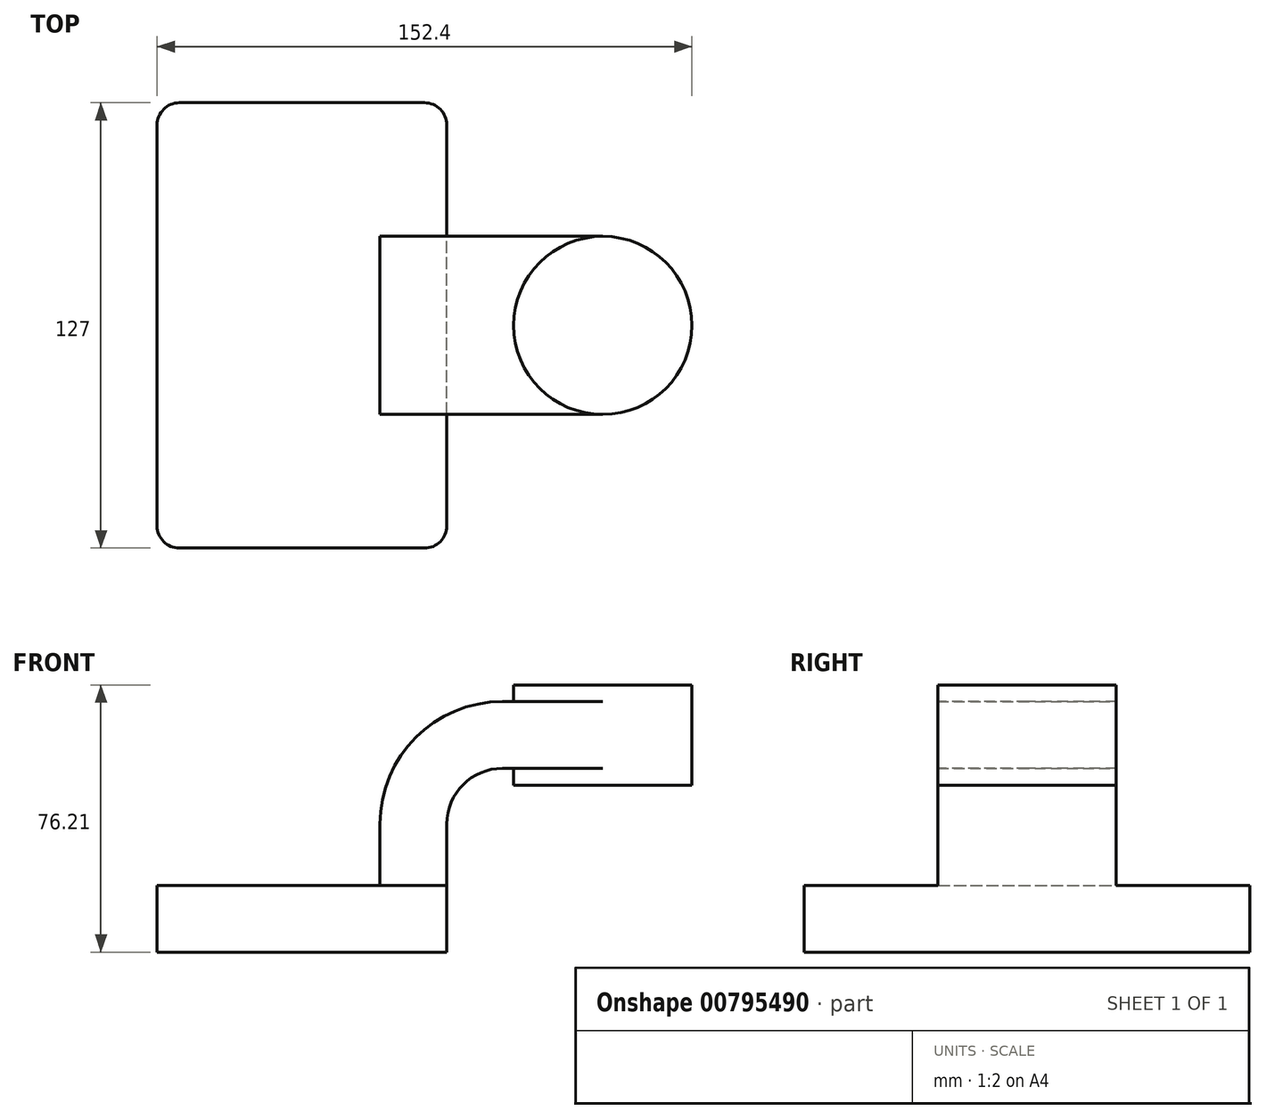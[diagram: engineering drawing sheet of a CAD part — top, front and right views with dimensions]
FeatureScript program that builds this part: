
annotation { "Feature Type Name" : "Feature", "Feature Type Description" : "" }
export const myFeature = defineFeature(function(context is Context, id is Id, definition is map)
    precondition{}
    {
        {
            var Q0;
            Q0=qCreatedBy(makeId("Front.planeOp"),FACE);
            var sketch = newSketch(context, id + "F0", { "sketchPlane" : qUnion([Q0])});
            skLineSegment(sketch, "E0.bottom", {"start": v(-41.28, 9.52) * mm, "end": v(41.27, 9.53) * mm});
            skLineSegment(sketch, "E0.top", {"start": v(-41.27, -9.52) * mm, "end": v(41.28, -9.52) * mm});
            skLineSegment(sketch, "E0.left", {"start": v(-41.28, 9.52) * mm, "end": v(-41.27, -9.53) * mm});
            skLineSegment(sketch, "E0.right", {"start": v(41.28, 9.53) * mm, "end": v(41.28, -9.52) * mm});
            skPoint(sketch, "E0.middle", {"position": v(0, 0) * mm});
            skLineSegment(sketch, "E1.bottom", {"start": v(111.13, 38.1) * mm, "end": v(60.33, 38.1) * mm});
            skLineSegment(sketch, "E1.top", {"start": v(111.13, 66.68) * mm, "end": v(60.33, 66.67) * mm});
            skLineSegment(sketch, "E1.left", {"start": v(111.13, 38.1) * mm, "end": v(111.13, 66.68) * mm});
            skLineSegment(sketch, "E1.right", {"start": v(60.33, 38.1) * mm, "end": v(60.33, 66.68) * mm});
            skPoint(sketch, "E1.middle", {"position": v(85.73, 52.39) * mm});
            skLineSegment(sketch, "E2", {"start": v(41.27, 9.53) * mm, "end": v(41.27, 27) * mm});
            skArc(sketch, "E3", {"start": v(41.27, 27) * mm, "mid": v(45.92, 38.23) * mm, "end": v(57.15, 42.88) * mm});
            skLineSegment(sketch, "E4", {"start": v(57.15, 42.88) * mm, "end": v(85.73, 42.88) * mm});
            skLineSegment(sketch, "E5.0", {"start": v(57.15, 61.93) * mm, "end": v(85.72, 61.93) * mm});
            skArc(sketch, "E5.1", {"start": v(22.23, 27) * mm, "mid": v(32.45, 51.7) * mm, "end": v(57.15, 61.93) * mm});
            skLineSegment(sketch, "E5.2", {"start": v(22.22, 9.53) * mm, "end": v(22.22, 27) * mm});
            skFitSpline(sketch, "E6", {"points": [v(-41.28, 9.52) * mm, v(57.15, 61.93) * mm], "startDerivative": vector(47.12, 132.78) * mm, "endDerivative": vector(118.1, -13.42) * mm});
            skLineSegment(sketch, "E7", {"start": v(85.73, 38.1) * mm, "end": v(85.73, 66.68) * mm});
            skSolve(sketch);
        }
        {
            var Q0;
            Q0=makeQuery(id+"F0.imprint","IMPRINT",FACE,{"disambiguationData":[TD([[makeQuery(id+"F0.imprint","IMPRINT",EDGE,{"derivedFrom":sQuery(id+"F0.wireOp",EDGE,"E0.top")}),1.0]])]});
            extrude(context, id + "F1", {"entities" : qUnion([Q0]), "endBound" : BoundingType.SYMMETRIC, "depth" : 127 * mm, "offsetDistance" : 25.4 * mm});
        }
        {
            var Q0;
            {var subQ1=sQuery(id+"F0.wireOp",EDGE,"E2");Q0=makeQuery(id+"F0.imprint","IMPRINT",FACE,{"disambiguationData":[TD([[makeQuery(id+"F0.imprint","IMPRINT",EDGE,{"derivedFrom":subQ1}),1.0]])]});}
            var Q1;
            {var subQ0=sQuery(id+"F0.wireOp",EDGE,"E4");var subQ1=sQuery(id+"F0.wireOp",EDGE,"E1.right");var subQ2=makeQuery(id+"F0.imprint","INTERSECT",VERTEX,{"derivedFrom":[subQ1,subQ0]});Q1=makeQuery(id+"F0.imprint","IMPRINT",FACE,{"disambiguationData":[TD([[makeQuery(id+"F0.imprint","IMPRINT",EDGE,{"disambiguationData":[TD([[subQ2,-1.0]])],"derivedFrom":subQ1}),-1.0]])]});}
            extrude(context, id + "F2", {"entities" : qUnion([Q0, Q1]), "operationType" : NewBodyOperationType.ADD, "endBound" : BoundingType.SYMMETRIC, "depth" : 50.8 * mm, "offsetDistance" : 25.4 * mm});
        }
        {
            var Q0;
            Q0=makeQuery(id+"F0.imprint","IMPRINT",FACE,{"disambiguationData":[TD([[makeQuery(id+"F0.imprint","IMPRINT",EDGE,{"derivedFrom":sQuery(id+"F0.wireOp",EDGE,"E5.1")}),1.0]])]});
            extrude(context, id + "F3", {"entities" : qUnion([Q0]), "operationType" : NewBodyOperationType.ADD, "endBound" : BoundingType.SYMMETRIC, "depth" : 15.88 * mm, "offsetDistance" : 25.4 * mm});
        }
        {
            var Q0;
            {var subQ0=sQuery(id+"F0.wireOp",EDGE,"E1.left");Q0=makeQuery(id+"F0.imprint","IMPRINT",FACE,{"disambiguationData":[TD([[makeQuery(id+"F0.imprint","IMPRINT",EDGE,{"derivedFrom":subQ0}),1.0]])]});}
            var Q1;
            Q1=sQuery(id+"F0.wireOp",EDGE,"E7");
            revolve(context, id + "F4", {"operationType" : NewBodyOperationType.ADD, "surfaceOperationType" : NewSurfaceOperationType.NEW, "entities" : qUnion([Q0]), "axis" : qUnion([Q1]), "revolveType" : RevolveType.FULL});
        }
        {
            var Q0;
            Q0=makeQuery(id+"F1.opExtrude","CAP_EDGE",EDGE,{"disambiguationData":[OSD([sQuery(id+"F0.wireOp",EDGE,"E0.left")])],"isStart":false});
            var Q1;
            Q1=makeQuery(id+"F1.opExtrude","CAP_EDGE",EDGE,{"disambiguationData":[OSD([sQuery(id+"F0.wireOp",EDGE,"E0.right")])],"isStart":false});
            var Q2;
            Q2=makeQuery(id+"F1.opExtrude","CAP_EDGE",EDGE,{"disambiguationData":[OSD([sQuery(id+"F0.wireOp",EDGE,"E0.right")])],"isStart":true});
            var Q3;
            Q3=makeQuery(id+"F1.opExtrude","CAP_EDGE",EDGE,{"disambiguationData":[OSD([sQuery(id+"F0.wireOp",EDGE,"E0.left")])],"isStart":true});
            fillet(context, id + "F5", {"entities" : qUnion([Q0, Q1, Q2, Q3]), "radius" : 6.35 * mm, "tangentPropagation" : true, "allowEdgeOverflow" : false});
        }
    });
